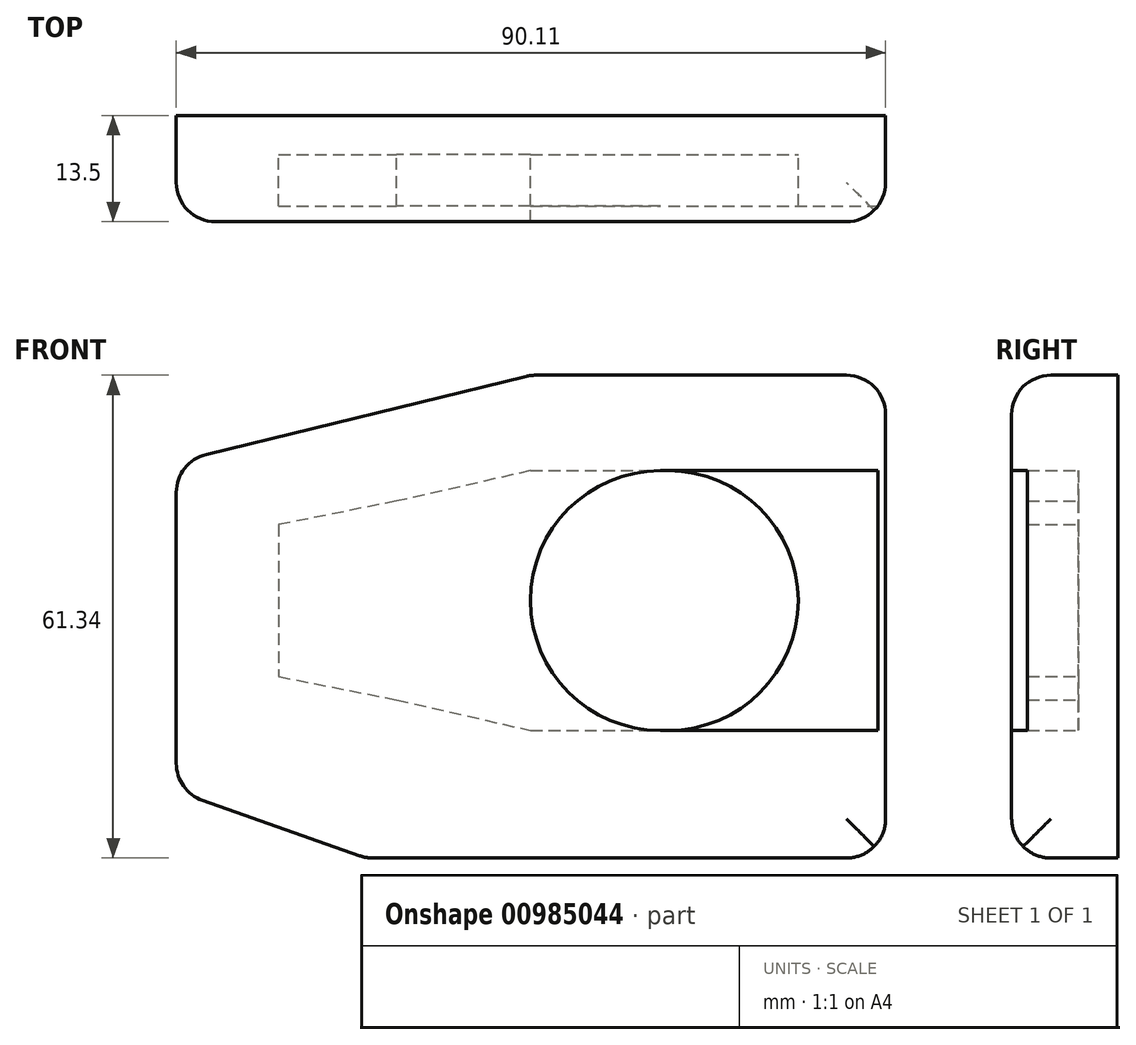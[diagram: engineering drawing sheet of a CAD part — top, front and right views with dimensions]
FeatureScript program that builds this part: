
annotation { "Feature Type Name" : "Feature", "Feature Type Description" : "" }
export const myFeature = defineFeature(function(context is Context, id is Id, definition is map)
    precondition{}
    {
        {
            var Q0;
            Q0=qCreatedBy(makeId("Front.planeOp"),FACE);
            var sketch = newSketch(context, id + "F0", { "sketchPlane" : qUnion([Q0])});
            skLineSegment(sketch, "E0.bottom", {"start": v(0, 16.5) * mm, "end": v(17.5, 16.5) * mm});
            skLineSegment(sketch, "E0.top", {"start": v(0, -16.5) * mm, "end": v(17.5, -16.5) * mm});
            skLineSegment(sketch, "E1.right", {"start": v(-32, 9.65) * mm, "end": v(-32, -9.65) * mm});
            skLineSegment(sketch, "E2", {"start": v(-32, 2.54) * mm, "end": v(-0.13, 2.54) * mm, "construction": true});
            skLineSegment(sketch, "E3", {"start": v(-32, -4.97) * mm, "end": v(7.5, -4.97) * mm, "construction": true});
            skArc(sketch, "E4", {"start": v(17.5, -16.5) * mm, "mid": v(34, 0) * mm, "end": v(17.5, 16.5) * mm});
            skLineSegment(sketch, "E5", {"start": v(0, 16.5) * mm, "end": v(-17, 12.62) * mm});
            skLineSegment(sketch, "E6", {"start": v(-17, 12.62) * mm, "end": v(-32, 9.65) * mm});
            skLineSegment(sketch, "E7", {"start": v(-32, -9.65) * mm, "end": v(-17, -12.63) * mm});
            skLineSegment(sketch, "E8", {"start": v(-17, -12.63) * mm, "end": v(0, -16.5) * mm});
            skLineSegment(sketch, "E9", {"start": v(31.07, 28.63) * mm, "end": v(0, 28.63) * mm});
            skLineSegment(sketch, "E10", {"start": v(0, 28.63) * mm, "end": v(-45, 17.65) * mm});
            skLineSegment(sketch, "E11", {"start": v(-45, 17.65) * mm, "end": v(-45, -24.21) * mm});
            skLineSegment(sketch, "E12", {"start": v(-45, -24.21) * mm, "end": v(-20.9, -32.71) * mm});
            skLineSegment(sketch, "E13", {"start": v(-20.9, -32.71) * mm, "end": v(45.11, -32.71) * mm});
            skLineSegment(sketch, "E14", {"start": v(45.11, -32.71) * mm, "end": v(45.11, 28.63) * mm});
            skLineSegment(sketch, "E15", {"start": v(45.11, 28.63) * mm, "end": v(31.07, 28.63) * mm});
            skSolve(sketch);
        }
        {
            var Q0;
            Q0=makeQuery(id+"F0.imprint","IMPRINT",FACE,{"disambiguationData":[TD([[makeQuery(id+"F0.imprint","IMPRINT",EDGE,{"derivedFrom":sQuery(id+"F0.wireOp",EDGE,"E0.bottom")}),1.0]])]});
            extrude(context, id + "F1", {"entities" : qUnion([Q0]), "depth" : 6.5 * mm, "offsetDistance" : 25 * mm});
        }
        {
            var Q0;
            Q0=makeQuery(id+"F0.imprint","IMPRINT",FACE,{"disambiguationData":[TD([[makeQuery(id+"F0.imprint","IMPRINT",EDGE,{"derivedFrom":sQuery(id+"F0.wireOp",EDGE,"E0.bottom")}),-1.0]])]});
            var Q1;
            Q1=makeQuery(id+"F0.imprint","IMPRINT",FACE,{"disambiguationData":[TD([[makeQuery(id+"F0.imprint","IMPRINT",EDGE,{"derivedFrom":sQuery(id+"F0.wireOp",EDGE,"E0.bottom")}),1.0]])]});
            extrude(context, id + "F2", {"entities" : qUnion([Q0, Q1]), "operationType" : NewBodyOperationType.ADD, "oppositeDirection" : true, "depth" : 5 * mm, "offsetDistance" : 25 * mm});
        }
        {
            var Q0;
            Q0=makeQuery(id+"F1.opExtrude","CAP_FACE",FACE,{"disambiguationData":[OSD([sQuery(id+"F0.wireOp",EDGE,"E0.bottom"),sQuery(id+"F0.wireOp",EDGE,"E0.top"),sQuery(id+"F0.wireOp",EDGE,"E1.right"),sQuery(id+"F0.wireOp",EDGE,"E4"),sQuery(id+"F0.wireOp",EDGE,"E5"),sQuery(id+"F0.wireOp",EDGE,"E6"),sQuery(id+"F0.wireOp",EDGE,"E7"),sQuery(id+"F0.wireOp",EDGE,"E8"),sQuery(id+"F0.wireOp",EDGE,"E9"),sQuery(id+"F0.wireOp",EDGE,"E10"),sQuery(id+"F0.wireOp",EDGE,"E11"),sQuery(id+"F0.wireOp",EDGE,"E12"),sQuery(id+"F0.wireOp",EDGE,"E13"),sQuery(id+"F0.wireOp",EDGE,"E14"),sQuery(id+"F0.wireOp",EDGE,"E15")])],"isStart":false});
            var sketch = newSketch(context, id + "F3", { "sketchPlane" : qUnion([Q0])});
            skLineSegment(sketch, "E16.0", {"start": v(0, 28.63) * mm, "end": v(-45, 17.65) * mm});
            skLineSegment(sketch, "E16.1", {"start": v(-45, 17.65) * mm, "end": v(-45, -24.21) * mm});
            skLineSegment(sketch, "E16.2", {"start": v(-45, -24.21) * mm, "end": v(-20.9, -32.71) * mm});
            skLineSegment(sketch, "E16.3", {"start": v(-20.9, -32.71) * mm, "end": v(45.11, -32.71) * mm});
            skLineSegment(sketch, "E17.0", {"start": v(31.07, 28.63) * mm, "end": v(0, 28.63) * mm});
            skLineSegment(sketch, "E17.1", {"start": v(45.11, 28.63) * mm, "end": v(31.07, 28.63) * mm});
            skLineSegment(sketch, "E17.2", {"start": v(45.11, -32.71) * mm, "end": v(45.11, 28.63) * mm});
            skArc(sketch, "E18", {"start": v(16.5, 16.5) * mm, "mid": v(0, 0) * mm, "end": v(16.5, -16.5) * mm});
            skLineSegment(sketch, "E19", {"start": v(16.5, 16.5) * mm, "end": v(45.11, 16.5) * mm});
            skLineSegment(sketch, "E20", {"start": v(16.5, -16.5) * mm, "end": v(45.11, -16.5) * mm});
            skPoint(sketch, "E21.orphan", {"position": v(8.75, -16.5) * mm});
            skSolve(sketch);
        }
        {
            var Q0;
            {var subQ12=sQuery(id+"F0.wireOp",EDGE,"E1.right");Q0=makeQuery(id+"F3.imprint","IMPRINT",FACE,{"disambiguationData":[TD([[makeQuery(id+"F3.imprint","IMPRINT",EDGE,{"derivedFrom":makeQuery(id+"F1.opExtrude","CAP_EDGE",EDGE,{"disambiguationData":[OSD([subQ12])],"isStart":false})}),-1.0]])]});}
            var Q1;
            {var subQ2=sQuery(id+"F3.wireOp",EDGE,"E18");Q1=makeQuery(id+"F3.imprint","IMPRINT",FACE,{"disambiguationData":[TD([[makeQuery(id+"F3.imprint","IMPRINT",EDGE,{"derivedFrom":subQ2}),-1.0]])]});}
            extrude(context, id + "F4", {"entities" : qUnion([Q0, Q1]), "operationType" : NewBodyOperationType.ADD, "depth" : 2 * mm, "offsetDistance" : 25 * mm});
        }
        {
            var Q0;
            {var subQ0=sQuery(id+"F0.wireOp",EDGE,"E15");var subQ1=sQuery(id+"F0.wireOp",EDGE,"E14");Q0=makeQuery(id+"F2.boolean.opBoolean","MERGE",EDGE,{"derivedFrom":[makeQuery(id+"F1.opExtrude","SWEPT_EDGE",EDGE,{"disambiguationData":[OSD([subQ1,subQ0])]}),makeQuery(id+"F2.opExtrude","SWEPT_EDGE",EDGE,{"disambiguationData":[OSD([subQ1,subQ0])]})]});}
            var Q1;
            {var subQ0=sQuery(id+"F0.wireOp",EDGE,"E14");var subQ1=sQuery(id+"F0.wireOp",EDGE,"E13");Q1=makeQuery(id+"F2.boolean.opBoolean","MERGE",EDGE,{"derivedFrom":[makeQuery(id+"F1.opExtrude","SWEPT_EDGE",EDGE,{"disambiguationData":[OSD([subQ1,subQ0])]}),makeQuery(id+"F2.opExtrude","SWEPT_EDGE",EDGE,{"disambiguationData":[OSD([subQ1,subQ0])]})]});}
            var Q2;
            {var subQ0=sQuery(id+"F0.wireOp",EDGE,"E12");var subQ1=sQuery(id+"F0.wireOp",EDGE,"E11");Q2=makeQuery(id+"F2.boolean.opBoolean","MERGE",EDGE,{"derivedFrom":[makeQuery(id+"F1.opExtrude","SWEPT_EDGE",EDGE,{"disambiguationData":[OSD([subQ1,subQ0])]}),makeQuery(id+"F2.opExtrude","SWEPT_EDGE",EDGE,{"disambiguationData":[OSD([subQ1,subQ0])]})]});}
            var Q3;
            {var subQ0=sQuery(id+"F0.wireOp",EDGE,"E11");var subQ1=sQuery(id+"F0.wireOp",EDGE,"E10");Q3=makeQuery(id+"F2.boolean.opBoolean","MERGE",EDGE,{"derivedFrom":[makeQuery(id+"F1.opExtrude","SWEPT_EDGE",EDGE,{"disambiguationData":[OSD([subQ1,subQ0])]}),makeQuery(id+"F2.opExtrude","SWEPT_EDGE",EDGE,{"disambiguationData":[OSD([subQ1,subQ0])]})]});}
            var Q4;
            {var subQ0=sQuery(id+"F0.wireOp",EDGE,"E10");var subQ1=sQuery(id+"F0.wireOp",EDGE,"E9");Q4=makeQuery(id+"F2.boolean.opBoolean","MERGE",EDGE,{"derivedFrom":[makeQuery(id+"F1.opExtrude","SWEPT_EDGE",EDGE,{"disambiguationData":[OSD([subQ1,subQ0])]}),makeQuery(id+"F2.opExtrude","SWEPT_EDGE",EDGE,{"disambiguationData":[OSD([subQ1,subQ0])]})]});}
            var Q5;
            {var subQ0=sQuery(id+"F0.wireOp",EDGE,"E13");var subQ1=sQuery(id+"F0.wireOp",EDGE,"E12");Q5=makeQuery(id+"F2.boolean.opBoolean","MERGE",EDGE,{"derivedFrom":[makeQuery(id+"F1.opExtrude","SWEPT_EDGE",EDGE,{"disambiguationData":[OSD([subQ1,subQ0])]}),makeQuery(id+"F2.opExtrude","SWEPT_EDGE",EDGE,{"disambiguationData":[OSD([subQ1,subQ0])]})]});}
            var Q6;
            Q6=makeQuery(id+"F4.opExtrude","CAP_EDGE",EDGE,{"disambiguationData":[OSD([sQuery(id+"F3.wireOp",EDGE,"E16.2")])],"isStart":false});
            var Q7;
            Q7=makeQuery(id+"F4.opExtrude","CAP_EDGE",EDGE,{"disambiguationData":[OSD([sQuery(id+"F3.wireOp",EDGE,"E16.3")])],"isStart":false});
            var Q8;
            Q8=makeQuery(id+"F4.opExtrude","CAP_EDGE",EDGE,{"disambiguationData":[OSD([sQuery(id+"F3.wireOp",EDGE,"E16.1")])],"isStart":false});
            var Q9;
            Q9=makeQuery(id+"F4.opExtrude","CAP_EDGE",EDGE,{"disambiguationData":[OSD([sQuery(id+"F3.wireOp",EDGE,"E16.0")])],"isStart":false});
            var Q10;
            Q10=makeQuery(id+"F4.opExtrude","CAP_EDGE",EDGE,{"disambiguationData":[OSD([sQuery(id+"F3.wireOp",EDGE,"E17.0"),sQuery(id+"F3.wireOp",EDGE,"E17.1")])],"isStart":false});
            var Q11;
            {var subQ0=sQuery(id+"F3.wireOp",EDGE,"E17.2");Q11=makeQuery(id+"F4.opExtrude","CAP_EDGE",EDGE,{"disambiguationData":[OSD([subQ0]),TDD([makeQuery(id+"F3.imprint","IMPRINT",EDGE,{"disambiguationData":[TD([[makeQuery(id+"F3.imprint","INTERSECT",VERTEX,{"derivedFrom":[sQuery(id+"F3.wireOp",EDGE,"E17.1"),subQ0]}),1.0]])],"derivedFrom":subQ0})])],"isStart":false});}
            fillet(context, id + "F5", {"entities" : qUnion([Q0, Q1, Q2, Q3, Q4, Q5, Q6, Q7, Q8, Q9, Q10, Q11]), "radius" : 5 * mm, "tangentPropagation" : true, "allowEdgeOverflow" : false});
        }
    });
